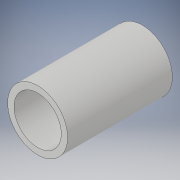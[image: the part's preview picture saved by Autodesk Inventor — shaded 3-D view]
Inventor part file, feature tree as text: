
AUTODESK INVENTOR PART (.ipt)
format: ipt  version: 2017 (Build 210142000, 142)  size: 95,744 bytes
history: native  units: in
note: dims shown in document units (in); Inventor stores cm internally (conversion verified against a paired STEP export)
features: extrude x1, sketch x1
ambient origin geometry x8: Origin, YZ Plane, XZ Plane, XY Plane, X Axis, Y Axis, Z Axis, Center Point
bodies: Solid1 (feature_tree)
feature tree (2):
  extrude  "Extrusion1"  Depth=0.698in
  sketch  "Sketch1"  dims[d0=0.315in d1=0.4in d2=0.698in d3=0.0in]
